# Revit family: Hager-Orion_Plus-IP65-D160-H160mm-Cl.I-Steel_encl-630A-NoHosted-PT-pt
name_source: partatom
category: Equipement électrique
units: mm (PartAtom-declared; Revit-internal decimal feet)

## family parameters
Basée sur le plan de construction = Oui
Configuration du panneau = Deux colonnes, circuits au sein
Cote de connecteur circulaire = Utiliser le diamètre
Couper avec des vides une fois chargée = Non
Partagée = Non
Point de calcul de pièce = Non
Toujours verticalement = Oui
Type d'élément = Tableau de raccordement

## types (14) — shared parameters
Commentaires du type = Orion Plus
EF000003 - Método de montagem = EV000384 - Montagem em superfície (gesso)
EF000007 - Cor = EV000270 - Cinzento
EF000049 - Profundidade = 160 mm  [stored 0.524934 ft]
EF000116 - Número RAL = 7035
EF000118 - Com tampa de montagem = Non
EF000437 - Número de entradas de condutores = 2
EF001596 - Material do corpo = EV000179 - Aço
EF001613 - Integridade do circuito = EV000494 - Nenhum
EF003532 - Adequado para uso no exterior = Non
EF004293 - Força de impacto = EV008784 - IK10
EF004464 - Tipo de porta = EV002646 - Único
EF005474 - Grau de proteção (IP) = EV006421 - IP65
EF006306 - Com fecho = Oui
EF007800 - Adequado para proteção contra raios = Non
EF008873 - Corrente nominal (In) = 630 A
EF009171 - Espessura do material da porta/tampa = 2 mm  [stored 0.00656168 ft]
EF015940 - Tampa com libertação de sobrepressão = Non
Elévation par défaut = 1219 mm
Fabricant = Hager
HG000002 - Com porta ou tampa = Oui
HG000003 - Gama = Orion Plus
HG000006 - Encastrado = Non
HG000009 - Porta dupla = Non
HG000010 - Portas assimétricas = Non
HG000023 - Recinto de secção dupla = Non
HG000024 - Altura da secção inferior = 600 mm
HG000026 - Instalação no chão = Non
zero-valued in all types: EF000218 - Profundidade incorporada, HG000027 - Altura da Plinta

## per-type parameters (varying)
| type | EF000008 - Largura | EF000040 - Altura | EF000266 - Número de linhas | EF000339 - Tipo de difusor | EF001088 - Extensão possível | EF001131 - Profundidade interior | EF002950 - Largura em número de módulos | EF004427 - Número de módulos | EF006244 - Tampa/porta transparente | EF009170 - Espessura do material do invólucro | EF009212 - Tipo de tampa | EF009554 - Número de aberturas para placas de flange | HG000004 - Referência do Fabricante |
| Montagem em superfície (gesso) IP65 L200 A250 P160  - FL101A | 200 mm  [stored 0.656168 ft] | 250 mm  [stored 0.82021 ft] | 0 | EV004216 - Porta | Non | 160 mm  [stored 0.524934 ft] | 0 | 0 | Non | 2 mm  [stored 0.00656168 ft] | EV009916 - Com recuo | 2 | FL101A |
| Montagem em superfície (gesso) IP65 L200 A250 P160  - FL151A | 200 mm  [stored 0.656168 ft] | 250 mm  [stored 0.82021 ft] | 0 | EV004216 - Porta | Non | 160 mm  [stored 0.524934 ft] | 0 | 0 | Oui | 2 mm  [stored 0.00656168 ft] | EV009916 - Com recuo | 2 | FL151A |
| Montagem em superfície (gesso) IP65 L250 A300 P160  - FL102A | 250 mm  [stored 0.82021 ft] | 300 mm | 1 | EV004216 - Porta | Oui | 160 mm  [stored 0.524934 ft] | 0 | 0 | Non | 2 mm  [stored 0.00656168 ft] | EV009916 - Com recuo | 2 | FL102A |
| Montagem em superfície (gesso) IP65 L250 A300 P160  - FL152A | 250 mm  [stored 0.82021 ft] | 300 mm | 0 | EV004216 - Porta | Oui | 160 mm  [stored 0.524934 ft] | 0 | 0 | Oui | 1 mm  [stored 0.00328084 ft] | EV000116 - Fechado | 2 | FL152A |
| Montagem em superfície (gesso) IP65 L300 A300 P160  - FL103A | 300 mm | 300 mm | 0 | EV004216 - Porta | Non | 160 mm  [stored 0.524934 ft] | 0 | 0 | Non | 2 mm  [stored 0.00656168 ft] | EV009916 - Com recuo | 2 | FL103A |
| Montagem em superfície (gesso) IP65 L300 A300 P160  - FL153A | 300 mm | 300 mm | 0 | EV004216 - Porta | Oui | 155 mm  [stored 0.50853 ft] | 0 | 0 | Oui | 2 mm  [stored 0.00656168 ft] | EV009916 - Com recuo | 2 | FL153A |
| Montagem em superfície (gesso) IP65 L300 A350 P160  - FL104A | 300 mm | 350 mm  [stored 1.14829 ft] | 2 | EV001012 - Tampa | Oui | 160 mm  [stored 0.524934 ft] | 10 | 20 | Non | 2 mm  [stored 0.00656168 ft] | EV000116 - Fechado | 2 | FL104A |
| Montagem em superfície (gesso) IP65 L300 A350 P160  - FL154A | 300 mm | 350 mm  [stored 1.14829 ft] | 2 | EV004216 - Porta | Oui | 160 mm  [stored 0.524934 ft] | 10 | 20 | Oui | 1 mm  [stored 0.00328084 ft] | EV000116 - Fechado | 2 | FL154A |
| Montagem em superfície (gesso) IP65 L300 A400 P160  - FL106A | 300 mm | 400 mm  [stored 1.31234 ft] | 0 | EV004216 - Porta | Non | 160 mm  [stored 0.524934 ft] | 0 | 0 | Non | 2 mm  [stored 0.00656168 ft] | EV009916 - Com recuo | 0 | FL106A |
| Montagem em superfície (gesso) IP65 L300 A400 P160  - FL156A | 300 mm | 400 mm  [stored 1.31234 ft] | 0 | EV004216 - Porta | Non | 160 mm  [stored 0.524934 ft] | 0 | 0 | Oui | 2 mm  [stored 0.00656168 ft] | EV009916 - Com recuo | 0 | FL156A |
| Montagem em superfície (gesso) IP65 L300 A500 P160  - FL109A | 300 mm | 500 mm  [stored 1.64042 ft] | 3 | EV004216 - Porta | Oui | 160 mm  [stored 0.524934 ft] | 10 | 30 | Non | 1 mm  [stored 0.00328084 ft] | EV000116 - Fechado | 2 | FL109A |
| Montagem em superfície (gesso) IP65 L300 A500 P160  - FL159A | 300 mm | 500 mm  [stored 1.64042 ft] | 3 | EV004216 - Porta | Oui | 160 mm  [stored 0.524934 ft] | 10 | 30 | Oui | 1 mm  [stored 0.00328084 ft] | EV000116 - Fechado | 2 | FL159A |
| Montagem em superfície (gesso) IP65 L400 A500 P160  - FL111A | 400 mm  [stored 1.31234 ft] | 500 mm  [stored 1.64042 ft] | 3 | EV004216 - Porta | Oui | 160 mm  [stored 0.524934 ft] | 16 | 54 | Non | 1 mm  [stored 0.00328084 ft] | EV000116 - Fechado | 2 | FL111A |
| Montagem em superfície (gesso) IP65 L400 A500 P160  - FL161A | 400 mm  [stored 1.31234 ft] | 500 mm  [stored 1.64042 ft] | 3 | EV004216 - Porta | Oui | 160 mm  [stored 0.524934 ft] | 16 | 54 | Oui | 1 mm  [stored 0.00328084 ft] | EV000116 - Fechado | 2 | FL161A |

note: [stored X ft] marks values corroborated as IEEE doubles in the binary element streams (Revit-internal decimal feet)

## geometry (parser evidence)
native form markers: Blend x4, Sweep x9
no freeform markers — native parametric forms only
